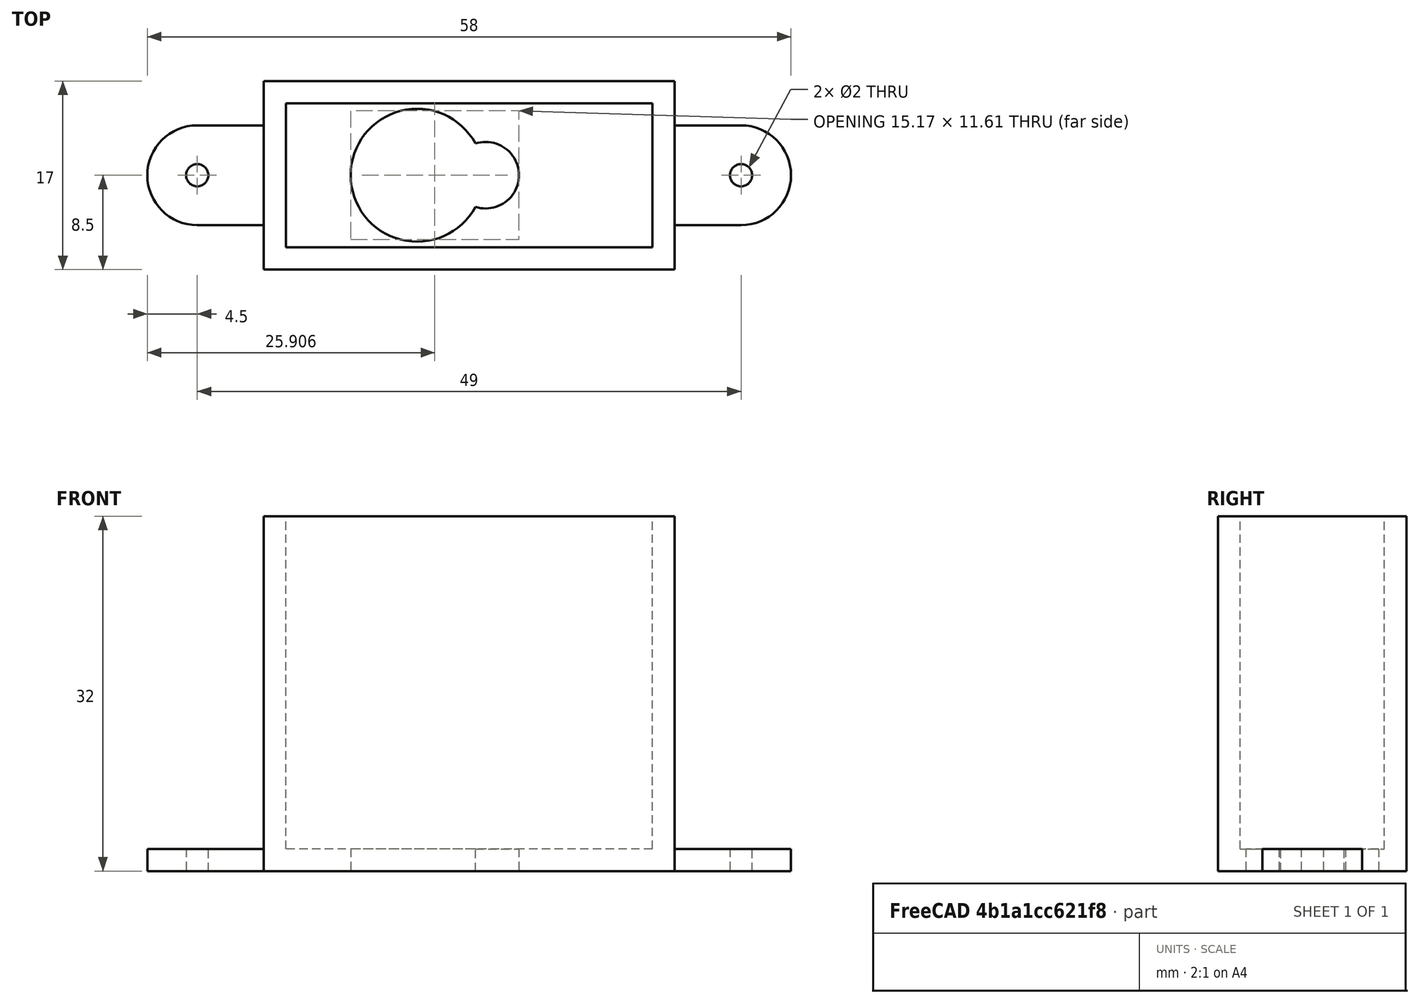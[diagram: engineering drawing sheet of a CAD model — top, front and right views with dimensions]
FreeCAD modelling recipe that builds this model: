
FCSTD DOCUMENT  (FreeCAD 0.18.4R)
Label: servo-housing
License: All rights reserved
LicenseURL: http://en.wikipedia.org/wiki/All_rights_reserved
objects: Sketcher::SketchObject×3, PartDesign::Pad×2, Mesh::Feature×1, PartDesign::Pocket×1, PartDesign::Body×1
note: 10 computed .brp shape members not serialized (recipe doc carries the construction recipe); baked Part::Feature solids carry a one-line shape summary decoded from their .brp

FEATURE [Sketcher::SketchObject] Sketch
  MapMode = 5
  Support = -> [XY_Plane]
  sketch-geometry (16):
    g0: LineSegment StartX=-18.5 StartY=8.5 StartZ=0 EndX=18.5 EndY=8.5 EndZ=0
    g1: LineSegment StartX=18.5 StartY=8.5 StartZ=0 EndX=18.5 EndY=4.5 EndZ=0
    g2: LineSegment StartX=18.5 StartY=-8.5 StartZ=0 EndX=-18.5 EndY=-8.5 EndZ=0
    g3: LineSegment StartX=-18.5 StartY=-8.5 StartZ=0 EndX=-18.5 EndY=-4.5 EndZ=0
    g4: ArcOfCircle CenterX=24.5 CenterY=-1e-16 CenterZ=0 NormalX=0 NormalY=0 NormalZ=1 AngleXU=0 Radius=4.5 StartAngle=4.71239 EndAngle=7.85398
    g5: LineSegment StartX=18.5 StartY=-4.5 StartZ=0 EndX=24.5 EndY=-4.5 EndZ=0
    g6: LineSegment StartX=18.5 StartY=4.5 StartZ=0 EndX=24.5 EndY=4.5 EndZ=0
    g7: LineSegment StartX=18.5 StartY=-4.5 StartZ=0 EndX=18.5 EndY=-8.5 EndZ=0
    g8: ArcOfCircle CenterX=-24.5 CenterY=-1e-16 CenterZ=0 NormalX=0 NormalY=0 NormalZ=1 AngleXU=0 Radius=4.5 StartAngle=1.5708 EndAngle=4.71239
    g9: LineSegment StartX=-18.5 StartY=4.5 StartZ=0 EndX=-24.5 EndY=4.5 EndZ=0
    g10: LineSegment StartX=-18.5 StartY=-4.5 StartZ=0 EndX=-24.5 EndY=-4.5 EndZ=0
    g11: LineSegment StartX=-18.5 StartY=4.5 StartZ=0 EndX=-18.5 EndY=8.5 EndZ=0
    g12: Circle CenterX=-24.5 CenterY=-1e-16 CenterZ=0 NormalX=0 NormalY=0 NormalZ=1 AngleXU=0 Radius=1
    g13: Circle CenterX=24.5 CenterY=-1e-16 CenterZ=0 NormalX=0 NormalY=0 NormalZ=1 AngleXU=0 Radius=1
    g14: ArcOfCircle CenterX=-4.69 CenterY=0 CenterZ=0 NormalX=0 NormalY=0 NormalZ=1 AngleXU=0 Radius=5.9885 StartAngle=0.497238 EndAngle=5.78595
    g15: ArcOfCircle CenterX=1.49 CenterY=0 CenterZ=0 NormalX=0 NormalY=0 NormalZ=1 AngleXU=0 Radius=3 StartAngle=4.40186 EndAngle=8.16451
  constraints (43):
    c: Coincident(g0,g1)
    c: Coincident(g7,g2)
    c: Coincident(g2,g3)
    c: Coincident(g11,g0)
    c: Horizontal(g0)
    c: Horizontal(g2)
    c: Vertical(g1)
    c: Coincident(g1,g6) = 1.5708
    c: Tangent(g5,g4) = -1.5708
    c: Tangent(g6,g4) = 1.5708
    c: Horizontal(g5)
    c: Tangent(g1,g7)
    c: Tangent(g9,g8) = -1.5708
    c: Tangent(g10,g8) = 1.5708
    c: Horizontal(g9)
    c: Tangent(g3,g11)
    c: Equal(g8,g4)
    c: Horizontal(g6)
    c: Coincident(g7,g5)
    c: Coincident(g9,g11)
    c: Coincident(g3,g10)
    c: Horizontal(g10)
    c: Symmetric(g2,g0,g-1)
    c: DistanceY(g2,g0) = 17
    c: DistanceX(g0,g0) = 37
    c: Equal(g6,g9)
    c: Symmetric(g9,g5,g-1)
    c: Horizontal(g8,g4)
    c: DistanceY(g3,g9) = 9
    c: DistanceX(g6,g6) = 6
    c: Coincident(g12,g8)
    c: Coincident(g13,g4)
    c: Equal(g13,g12)
    c: PointOnObject(g14,g-1)
    c: Radius(g14) = 5.9885
    c: Radius(g13) = 1
    c: PointOnObject(g15,g-1)
    c: Radius(g15) = 3
    c: Coincident(g15,g14)
    c: Coincident(g15,g14)
    c: DistanceX(g9,g14) = 13.81
    c: DistanceX(g14,g15) = 6.18
    c: Coincident(g15,g14)
FEATURE [PartDesign::Pad] Pad
  Length = 2
  Length2 = 100
  Profile = -> Sketch
  Type = 0
FEATURE [Mesh::Feature] MicroSG90_Servo_Motor  label="MicroSG90 Servo Motor"
  Placement = pos=(-11,6,25) rot=(-0.57735,0.57735,-0.57735;2.0944rad)
FEATURE [Sketcher::SketchObject] Sketch001
  ExternalGeometry = -> [Pad]
  MapMode = 5
  Placement = pos=(0,0,2) rot=(0,0,1;0rad)
  Support = -> [Pad]
  sketch-geometry (8):
    g0: LineSegment StartX=-18.5 StartY=8.5 StartZ=0 EndX=18.5 EndY=8.5 EndZ=0
    g1: LineSegment StartX=18.5 StartY=8.5 StartZ=0 EndX=18.5 EndY=-8.5 EndZ=0
    g2: LineSegment StartX=18.5 StartY=-8.5 StartZ=0 EndX=-18.5 EndY=-8.5 EndZ=0
    g3: LineSegment StartX=-18.5 StartY=-8.5 StartZ=0 EndX=-18.5 EndY=8.5 EndZ=0
    g4: LineSegment StartX=-16.5 StartY=6.5 StartZ=0 EndX=16.5 EndY=6.5 EndZ=0
    g5: LineSegment StartX=16.5 StartY=6.5 StartZ=0 EndX=16.5 EndY=-6.5 EndZ=0
    g6: LineSegment StartX=16.5 StartY=-6.5 StartZ=0 EndX=-16.5 EndY=-6.5 EndZ=0
    g7: LineSegment StartX=-16.5 StartY=-6.5 StartZ=0 EndX=-16.5 EndY=6.5 EndZ=0
  constraints (21):
    c: Coincident(g0,g1)
    c: Coincident(g1,g2)
    c: Coincident(g2,g3)
    c: Coincident(g3,g0)
    c: Horizontal(g0)
    c: Horizontal(g2)
    c: Vertical(g1)
    c: Vertical(g3)
    c: Coincident(g0,g-3)
    c: Coincident(g1,g-4)
    c: Coincident(g4,g5)
    c: Coincident(g5,g6)
    c: Coincident(g6,g7)
    c: Coincident(g7,g4)
    c: Horizontal(g4)
    c: Horizontal(g6)
    c: Vertical(g5)
    c: Vertical(g7)
    c: Symmetric(g5,g4,g-1)
    c: DistanceX(g4,g4) = 33
    c: DistanceY(g5,g5) = 13
FEATURE [PartDesign::Pad] Pad001
  BaseFeature = -> Pad
  Length = 30
  Length2 = 100
  Profile = -> Sketch001
  Type = 0
FEATURE [Sketcher::SketchObject] Sketch002
  ExternalGeometry = -> [Pad001]
  MapMode = 5
  Placement = pos=(18.5,0,0) rot=(0.57735,0.57735,0.57735;2.0944rad)
  Support = -> [Pad001]
  sketch-geometry (4):
    g0: ArcOfCircle CenterX=0 CenterY=27.5 CenterZ=0 NormalX=0 NormalY=0 NormalZ=1 AngleXU=0 Radius=1.5 StartAngle=3.14159 EndAngle=6.28319
    g1: LineSegment StartX=-1.5 StartY=32 StartZ=0 EndX=-1.5 EndY=27.5 EndZ=0
    g2: LineSegment StartX=1.5 StartY=32 StartZ=0 EndX=1.5 EndY=27.5 EndZ=0
    g3: LineSegment StartX=-1.5 StartY=32 StartZ=0 EndX=1.5 EndY=32 EndZ=0
  constraints (11):
    c: Tangent(g1,g0) = -1.5708
    c: Tangent(g2,g0) = 1.5708
    c: Vertical(g1)
    c: PointOnObject(g2,g-3)
    c: Vertical(g2)
    c: PointOnObject(g0,g-2)
    c: Radius(g0) = 1.5
    c: DistanceY(g2,g2) = 4.5
    c: PointOnObject(g1,g-3)
    c: Coincident(g3,g1)
    c: Coincident(g3,g2)
FEATURE [PartDesign::Pocket] Pocket
  BaseFeature = -> Pad001
  Length = 5
  Length2 = 100
  Profile = -> Sketch002
  Type = 0
FEATURE [PartDesign::Body] Body
  Group = -> [Sketch,Pad,Sketch001,Pad001,Sketch002,Pocket]
  Origin = -> Origin
  Tip = -> Pocket
